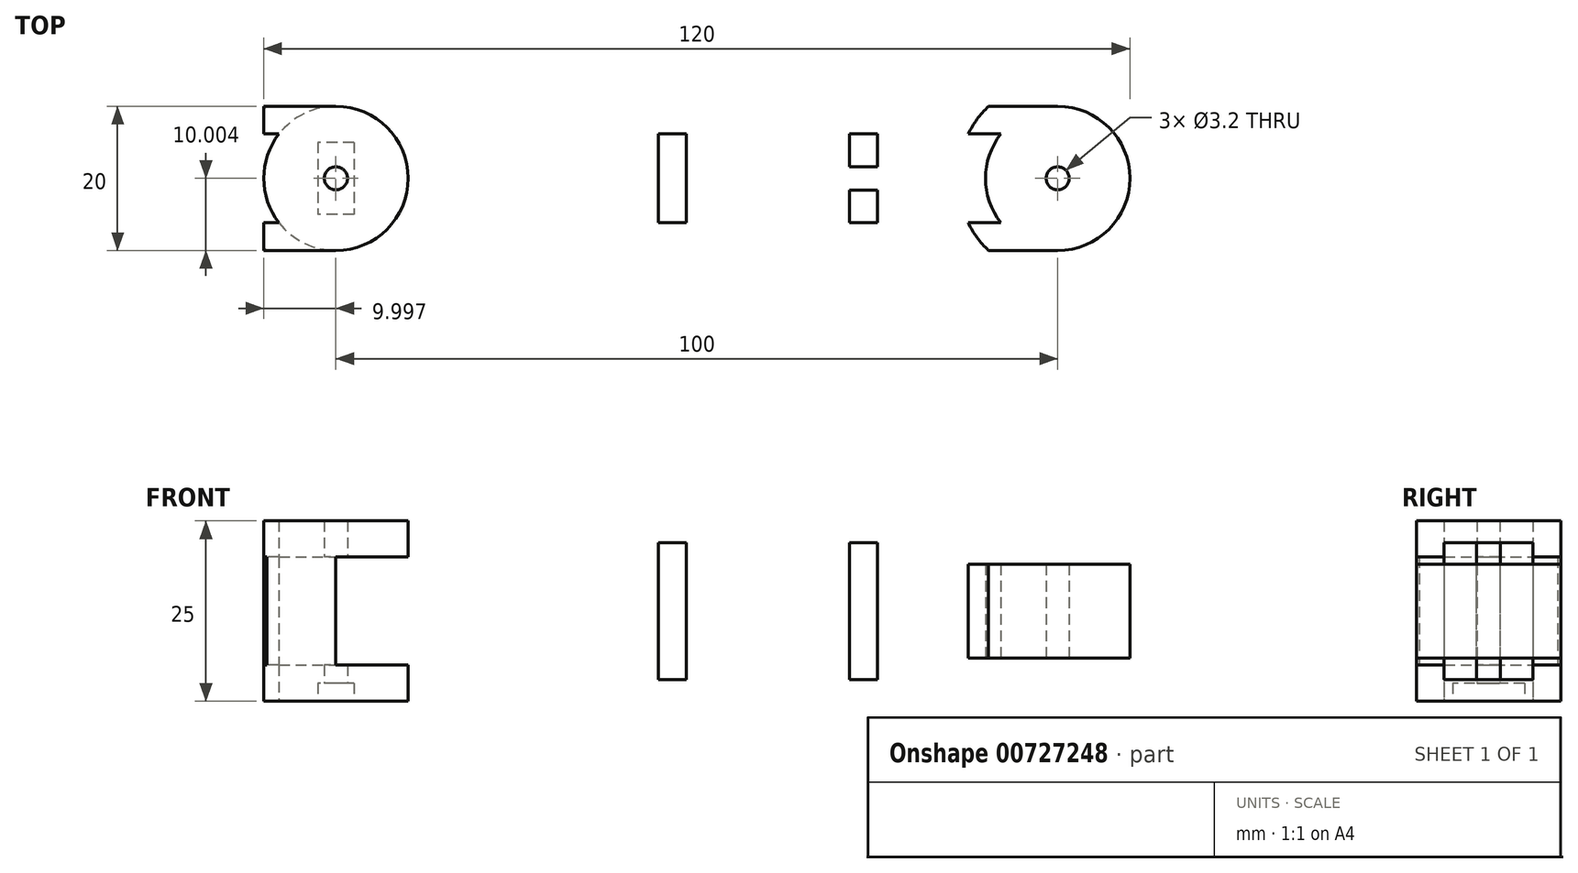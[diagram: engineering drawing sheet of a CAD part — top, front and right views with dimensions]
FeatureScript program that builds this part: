
annotation { "Feature Type Name" : "Feature", "Feature Type Description" : "" }
export const myFeature = defineFeature(function(context is Context, id is Id, definition is map)
    precondition{}
    {
        {
            var Q0;
            Q0=qCreatedBy(makeId("Top.planeOp"),FACE);
            var sketch = newSketch(context, id + "F0", { "sketchPlane" : qUnion([Q0])});
            skLineSegment(sketch, "E0.bottom", {"start": v(-96.42, 40.91) * mm, "end": v(23.58, 40.91) * mm});
            skLineSegment(sketch, "E0.top", {"start": v(-96.42, 20.91) * mm, "end": v(23.58, 20.91) * mm});
            skLineSegment(sketch, "E0.left", {"start": v(-96.42, 40.91) * mm, "end": v(-96.42, 20.91) * mm});
            skLineSegment(sketch, "E0.right", {"start": v(23.58, 40.91) * mm, "end": v(23.58, 20.91) * mm});
            skCircle(sketch, "E1", {"center": v(13.58, 30.91) * mm, "radius": 10 * mm});
            skPoint(sketch, "E1.centerSnap0", {"position": v(23.58, 30.91) * mm});
            skCircle(sketch, "E2", {"center": v(-86.42, 30.91) * mm, "radius": 10 * mm});
            skCircle(sketch, "E3", {"center": v(-86.42, 30.91) * mm, "radius": 1.6 * mm});
            skCircle(sketch, "E4", {"center": v(13.58, 30.91) * mm, "radius": 1.6 * mm});
            skLineSegment(sketch, "E5.0", {"start": v(-96.42, 37.06) * mm, "end": v(53.58, 37.06) * mm});
            skLineSegment(sketch, "E6.0", {"start": v(-96.42, 24.76) * mm, "end": v(53.58, 24.76) * mm});
            skCircle(sketch, "E7.0", {"center": v(-86.42, 30.91) * mm, "radius": 13.85 * mm});
            skCircle(sketch, "E8.0", {"center": v(13.58, 30.91) * mm, "radius": 13.85 * mm});
            skLineSegment(sketch, "E9", {"start": v(-15.27, 37.06) * mm, "end": v(-15.27, 24.76) * mm});
            skLineSegment(sketch, "E10", {"start": v(-11.42, 37.06) * mm, "end": v(-11.42, 24.76) * mm});
            skLineSegment(sketch, "E11", {"start": v(-41.72, 37.06) * mm, "end": v(-41.72, 24.76) * mm});
            skLineSegment(sketch, "E12", {"start": v(-37.87, 24.76) * mm, "end": v(-37.87, 37.06) * mm});
            skSolve(sketch);
        }
        {
            var Q0;
            {var subQ3=sQuery(id+"F0.wireOp",EDGE,"E7.0");var subQ4=sQuery(id+"F0.wireOp",EDGE,"E0.bottom");var subQ5=makeQuery(id+"F0.imprint","INTERSECT",VERTEX,{"disambiguationData":[OD(1.0)],"derivedFrom":[subQ4,subQ3]});Q0=makeQuery(id+"F0.imprint","IMPRINT",FACE,{"disambiguationData":[TD([[makeQuery(id+"F0.imprint","IMPRINT",EDGE,{"disambiguationData":[TD([[subQ5,-1.0]])],"derivedFrom":subQ4}),-1.0]])]});}
            var Q1;
            {var subQ0=sQuery(id+"F0.wireOp",EDGE,"E7.0");var subQ1=sQuery(id+"F0.wireOp",EDGE,"E0.bottom");var subQ2=makeQuery(id+"F0.imprint","INTERSECT",VERTEX,{"disambiguationData":[OD(1.0)],"derivedFrom":[subQ1,subQ0]});Q1=makeQuery(id+"F0.imprint","IMPRINT",FACE,{"disambiguationData":[TD([[makeQuery(id+"F0.imprint","IMPRINT",EDGE,{"disambiguationData":[TD([[subQ2,1.0]])],"derivedFrom":subQ1}),-1.0]])]});}
            var Q2;
            {var subQ0=sQuery(id+"F0.wireOp",EDGE,"E2");var subQ1=makeQuery(id+"F0.imprint","INTERSECT",VERTEX,{"derivedFrom":[sQuery(id+"F0.wireOp",EDGE,"E0.bottom"),subQ0]});Q2=makeQuery(id+"F0.imprint","IMPRINT",FACE,{"disambiguationData":[TD([[makeQuery(id+"F0.imprint","IMPRINT",EDGE,{"disambiguationData":[TD([[subQ1,1.0]])],"derivedFrom":subQ0}),1.0]])]});}
            var Q3;
            Q3=makeQuery(id+"F0.imprint","IMPRINT",FACE,{"disambiguationData":[TD([[makeQuery(id+"F0.imprint","IMPRINT",EDGE,{"derivedFrom":sQuery(id+"F0.wireOp",EDGE,"E3")}),-1.0]])]});
            var Q4;
            {var subQ0=sQuery(id+"F0.wireOp",EDGE,"E7.0");var subQ1=sQuery(id+"F0.wireOp",EDGE,"E0.top");var subQ2=makeQuery(id+"F0.imprint","INTERSECT",VERTEX,{"disambiguationData":[OD(1.0)],"derivedFrom":[subQ1,subQ0]});Q4=makeQuery(id+"F0.imprint","IMPRINT",FACE,{"disambiguationData":[TD([[makeQuery(id+"F0.imprint","IMPRINT",EDGE,{"disambiguationData":[TD([[subQ2,1.0]])],"derivedFrom":subQ1}),1.0]])]});}
            var Q5;
            {var subQ0=sQuery(id+"F0.wireOp",EDGE,"E2");var subQ1=makeQuery(id+"F0.imprint","INTERSECT",VERTEX,{"derivedFrom":[sQuery(id+"F0.wireOp",EDGE,"E0.top"),subQ0]});Q5=makeQuery(id+"F0.imprint","IMPRINT",FACE,{"disambiguationData":[TD([[makeQuery(id+"F0.imprint","IMPRINT",EDGE,{"disambiguationData":[TD([[subQ1,1.0]])],"derivedFrom":subQ0}),1.0]])]});}
            var Q6;
            {var subQ4=sQuery(id+"F0.wireOp",EDGE,"E7.0");var subQ6=sQuery(id+"F0.wireOp",EDGE,"E0.top");var subQ7=makeQuery(id+"F0.imprint","INTERSECT",VERTEX,{"disambiguationData":[OD(1.0)],"derivedFrom":[subQ6,subQ4]});Q6=makeQuery(id+"F0.imprint","IMPRINT",FACE,{"disambiguationData":[TD([[makeQuery(id+"F0.imprint","IMPRINT",EDGE,{"disambiguationData":[TD([[subQ7,-1.0]])],"derivedFrom":subQ6}),1.0]])]});}
            var Q7;
            {var subQ0=sQuery(id+"F0.wireOp",EDGE,"E11");Q7=makeQuery(id+"F0.imprint","IMPRINT",FACE,{"disambiguationData":[TD([[makeQuery(id+"F0.imprint","IMPRINT",EDGE,{"derivedFrom":subQ0}),1.0]])]});}
            var Q8;
            {var subQ0=sQuery(id+"F0.wireOp",EDGE,"E9");Q8=makeQuery(id+"F0.imprint","IMPRINT",FACE,{"disambiguationData":[TD([[makeQuery(id+"F0.imprint","IMPRINT",EDGE,{"derivedFrom":subQ0}),1.0]])]});}
            var Q9;
            Q9=makeQuery(id+"F0.imprint","IMPRINT",FACE,{"disambiguationData":[TD([[makeQuery(id+"F0.imprint","IMPRINT",EDGE,{"derivedFrom":sQuery(id+"F0.wireOp",EDGE,"E4")}),-1.0]])]});
            var Q10;
            {var subQ0=sQuery(id+"F0.wireOp",EDGE,"E1");var subQ1=makeQuery(id+"F0.imprint","INTERSECT",VERTEX,{"derivedFrom":[sQuery(id+"F0.wireOp",EDGE,"E0.bottom"),subQ0]});Q10=makeQuery(id+"F0.imprint","IMPRINT",FACE,{"disambiguationData":[TD([[makeQuery(id+"F0.imprint","IMPRINT",EDGE,{"disambiguationData":[TD([[subQ1,1.0]])],"derivedFrom":subQ0}),1.0]])]});}
            var Q11;
            {var subQ0=sQuery(id+"F0.wireOp",EDGE,"E8.0");var subQ1=sQuery(id+"F0.wireOp",EDGE,"E0.bottom");var subQ2=makeQuery(id+"F0.imprint","INTERSECT",VERTEX,{"disambiguationData":[OD(0.0)],"derivedFrom":[subQ1,subQ0]});Q11=makeQuery(id+"F0.imprint","IMPRINT",FACE,{"disambiguationData":[TD([[makeQuery(id+"F0.imprint","IMPRINT",EDGE,{"disambiguationData":[TD([[subQ2,-1.0]])],"derivedFrom":subQ1}),-1.0]])]});}
            var Q12;
            {var subQ0=sQuery(id+"F0.wireOp",EDGE,"E1");var subQ1=makeQuery(id+"F0.imprint","INTERSECT",VERTEX,{"derivedFrom":[sQuery(id+"F0.wireOp",EDGE,"E0.top"),subQ0]});Q12=makeQuery(id+"F0.imprint","IMPRINT",FACE,{"disambiguationData":[TD([[makeQuery(id+"F0.imprint","IMPRINT",EDGE,{"disambiguationData":[TD([[subQ1,1.0]])],"derivedFrom":subQ0}),1.0]])]});}
            var Q13;
            {var subQ0=sQuery(id+"F0.wireOp",EDGE,"E8.0");var subQ1=sQuery(id+"F0.wireOp",EDGE,"E0.top");var subQ2=makeQuery(id+"F0.imprint","INTERSECT",VERTEX,{"disambiguationData":[OD(0.0)],"derivedFrom":[subQ1,subQ0]});Q13=makeQuery(id+"F0.imprint","IMPRINT",FACE,{"disambiguationData":[TD([[makeQuery(id+"F0.imprint","IMPRINT",EDGE,{"disambiguationData":[TD([[subQ2,-1.0]])],"derivedFrom":subQ1}),1.0]])]});}
            extrude(context, id + "F1", {"entities" : qUnion([Q0, Q1, Q2, Q3, Q4, Q5, Q6, Q7, Q8, Q9, Q10, Q11, Q12, Q13]), "depth" : 25 * mm, "offsetDistance" : 25 * mm});
        }
        {
            var Q0;
            Q0=makeQuery(id+"F1.opExtrude","CAP_FACE",FACE,{"disambiguationData":[OSD([sQuery(id+"F0.wireOp",EDGE,"E0.bottom"),sQuery(id+"F0.wireOp",EDGE,"E0.top"),sQuery(id+"F0.wireOp",EDGE,"E1"),sQuery(id+"F0.wireOp",EDGE,"E2"),sQuery(id+"F0.wireOp",EDGE,"E3"),sQuery(id+"F0.wireOp",EDGE,"E4"),sQuery(id+"F0.wireOp",EDGE,"E5.0"),sQuery(id+"F0.wireOp",EDGE,"E6.0"),sQuery(id+"F0.wireOp",EDGE,"E9"),sQuery(id+"F0.wireOp",EDGE,"E10"),sQuery(id+"F0.wireOp",EDGE,"E11"),sQuery(id+"F0.wireOp",EDGE,"E12")])],"isStart":false});
            var sketch = newSketch(context, id + "F2", { "sketchPlane" : qUnion([Q0])});
            skLineSegment(sketch, "E13.bottom", {"start": v(-41.72, 37.06) * mm, "end": v(-37.87, 37.06) * mm});
            skLineSegment(sketch, "E13.top", {"start": v(-41.72, 24.76) * mm, "end": v(-37.87, 24.76) * mm});
            skLineSegment(sketch, "E13.left", {"start": v(-41.72, 37.06) * mm, "end": v(-41.72, 24.76) * mm});
            skLineSegment(sketch, "E13.right", {"start": v(-37.87, 37.06) * mm, "end": v(-37.87, 24.76) * mm});
            skLineSegment(sketch, "E14.bottom", {"start": v(-15.27, 37.06) * mm, "end": v(-11.42, 37.06) * mm});
            skLineSegment(sketch, "E14.top", {"start": v(-15.27, 24.76) * mm, "end": v(-11.42, 24.76) * mm});
            skLineSegment(sketch, "E14.left", {"start": v(-15.27, 37.06) * mm, "end": v(-15.27, 24.76) * mm});
            skLineSegment(sketch, "E14.right", {"start": v(-11.42, 37.06) * mm, "end": v(-11.42, 24.76) * mm});
            skSolve(sketch);
        }
        {
            var Q0;
            Q0 = qSketchRegion(id + "F2", true);
            extrude(context, id + "F3", {"entities" : qUnion([Q0]), "operationType" : NewBodyOperationType.REMOVE, "oppositeDirection" : true, "depth" : 3 * mm, "offsetDistance" : 25 * mm});
        }
        {
            var Q0;
            Q0=makeQuery(id+"F1.opExtrude","CAP_FACE",FACE,{"disambiguationData":[OSD([sQuery(id+"F0.wireOp",EDGE,"E0.bottom"),sQuery(id+"F0.wireOp",EDGE,"E0.top"),sQuery(id+"F0.wireOp",EDGE,"E1"),sQuery(id+"F0.wireOp",EDGE,"E2"),sQuery(id+"F0.wireOp",EDGE,"E3"),sQuery(id+"F0.wireOp",EDGE,"E4"),sQuery(id+"F0.wireOp",EDGE,"E5.0"),sQuery(id+"F0.wireOp",EDGE,"E6.0"),sQuery(id+"F0.wireOp",EDGE,"E9"),sQuery(id+"F0.wireOp",EDGE,"E10"),sQuery(id+"F0.wireOp",EDGE,"E11"),sQuery(id+"F0.wireOp",EDGE,"E12")])],"isStart":true});
            var sketch = newSketch(context, id + "F4", { "sketchPlane" : qUnion([Q0])});
            skLineSegment(sketch, "E15.bottom", {"start": v(-11.42, -37.06) * mm, "end": v(-15.27, -37.06) * mm});
            skLineSegment(sketch, "E15.top", {"start": v(-11.42, -24.76) * mm, "end": v(-15.27, -24.76) * mm});
            skLineSegment(sketch, "E15.left", {"start": v(-11.42, -37.06) * mm, "end": v(-11.42, -24.76) * mm});
            skLineSegment(sketch, "E15.right", {"start": v(-15.27, -37.06) * mm, "end": v(-15.27, -24.76) * mm});
            skLineSegment(sketch, "E16.bottom", {"start": v(-37.87, -37.06) * mm, "end": v(-41.72, -37.06) * mm});
            skLineSegment(sketch, "E16.top", {"start": v(-37.87, -24.76) * mm, "end": v(-41.72, -24.76) * mm});
            skLineSegment(sketch, "E16.left", {"start": v(-37.87, -37.06) * mm, "end": v(-37.87, -24.76) * mm});
            skLineSegment(sketch, "E16.right", {"start": v(-41.72, -37.06) * mm, "end": v(-41.72, -24.76) * mm});
            skSolve(sketch);
        }
        {
            var Q0;
            Q0 = qSketchRegion(id + "F4", true);
            extrude(context, id + "F5", {"entities" : qUnion([Q0]), "operationType" : NewBodyOperationType.REMOVE, "oppositeDirection" : true, "depth" : 3 * mm, "offsetDistance" : 25 * mm});
        }
        {
            var Q0;
            Q0=makeQuery(id+"F1.opExtrude","CAP_FACE",FACE,{"disambiguationData":[OSD([sQuery(id+"F0.wireOp",EDGE,"E0.bottom"),sQuery(id+"F0.wireOp",EDGE,"E0.top"),sQuery(id+"F0.wireOp",EDGE,"E1"),sQuery(id+"F0.wireOp",EDGE,"E2"),sQuery(id+"F0.wireOp",EDGE,"E3"),sQuery(id+"F0.wireOp",EDGE,"E4"),sQuery(id+"F0.wireOp",EDGE,"E5.0"),sQuery(id+"F0.wireOp",EDGE,"E6.0"),sQuery(id+"F0.wireOp",EDGE,"E9"),sQuery(id+"F0.wireOp",EDGE,"E10"),sQuery(id+"F0.wireOp",EDGE,"E11"),sQuery(id+"F0.wireOp",EDGE,"E12")])],"isStart":true});
            var sketch = newSketch(context, id + "F6", { "sketchPlane" : qUnion([Q0])});
            skPoint(sketch, "E17", {"position": v(-20.27, -39.81) * mm});
            skPoint(sketch, "E17.positionSnap0", {"position": v(-15.27, -39.81) * mm});
            skSolve(sketch);
        }
        {
            var Q0;
            {var subQ0=sQuery(id+"F0.wireOp",EDGE,"E1");var subQ1=makeQuery(id+"F0.imprint","INTERSECT",VERTEX,{"derivedFrom":[sQuery(id+"F0.wireOp",EDGE,"E0.top"),subQ0]});Q0=makeQuery(id+"F0.imprint","IMPRINT",FACE,{"disambiguationData":[TD([[makeQuery(id+"F0.imprint","IMPRINT",EDGE,{"disambiguationData":[TD([[subQ1,1.0]])],"derivedFrom":subQ0}),1.0]])]});}
            var Q1;
            Q1=makeQuery(id+"F0.imprint","IMPRINT",FACE,{"disambiguationData":[TD([[makeQuery(id+"F0.imprint","IMPRINT",EDGE,{"derivedFrom":sQuery(id+"F0.wireOp",EDGE,"E4")}),-1.0]])]});
            var Q2;
            {var subQ0=sQuery(id+"F0.wireOp",EDGE,"E1");var subQ1=makeQuery(id+"F0.imprint","INTERSECT",VERTEX,{"derivedFrom":[sQuery(id+"F0.wireOp",EDGE,"E0.bottom"),subQ0]});Q2=makeQuery(id+"F0.imprint","IMPRINT",FACE,{"disambiguationData":[TD([[makeQuery(id+"F0.imprint","IMPRINT",EDGE,{"disambiguationData":[TD([[subQ1,1.0]])],"derivedFrom":subQ0}),1.0]])]});}
            var Q3;
            {var subQ0=sQuery(id+"F0.wireOp",EDGE,"E8.0");var subQ1=sQuery(id+"F0.wireOp",EDGE,"E0.bottom");var subQ2=makeQuery(id+"F0.imprint","INTERSECT",VERTEX,{"disambiguationData":[OD(0.0)],"derivedFrom":[subQ1,subQ0]});Q3=makeQuery(id+"F0.imprint","IMPRINT",FACE,{"disambiguationData":[TD([[makeQuery(id+"F0.imprint","IMPRINT",EDGE,{"disambiguationData":[TD([[subQ2,-1.0]])],"derivedFrom":subQ1}),-1.0]])]});}
            var Q4;
            {var subQ0=sQuery(id+"F0.wireOp",EDGE,"E8.0");var subQ1=sQuery(id+"F0.wireOp",EDGE,"E0.top");var subQ2=makeQuery(id+"F0.imprint","INTERSECT",VERTEX,{"disambiguationData":[OD(0.0)],"derivedFrom":[subQ1,subQ0]});Q4=makeQuery(id+"F0.imprint","IMPRINT",FACE,{"disambiguationData":[TD([[makeQuery(id+"F0.imprint","IMPRINT",EDGE,{"disambiguationData":[TD([[subQ2,-1.0]])],"derivedFrom":subQ1}),1.0]])]});}
            extrude(context, id + "F7", {"entities" : qUnion([Q0, Q1, Q2, Q3, Q4]), "operationType" : NewBodyOperationType.REMOVE, "depth" : 25 * mm, "offsetDistance" : 25 * mm, "hasSecondDirection" : true, "secondDirectionOppositeDirection" : false, "secondDirectionDepth" : 19 * mm});
        }
        {
            var Q0;
            Q0=makeQuery(id+"F0.imprint","IMPRINT",FACE,{"disambiguationData":[TD([[makeQuery(id+"F0.imprint","IMPRINT",EDGE,{"derivedFrom":sQuery(id+"F0.wireOp",EDGE,"E4")}),-1.0]])]});
            var Q1;
            {var subQ0=sQuery(id+"F0.wireOp",EDGE,"E8.0");var subQ1=sQuery(id+"F0.wireOp",EDGE,"E0.bottom");var subQ2=makeQuery(id+"F0.imprint","INTERSECT",VERTEX,{"disambiguationData":[OD(0.0)],"derivedFrom":[subQ1,subQ0]});Q1=makeQuery(id+"F0.imprint","IMPRINT",FACE,{"disambiguationData":[TD([[makeQuery(id+"F0.imprint","IMPRINT",EDGE,{"disambiguationData":[TD([[subQ2,-1.0]])],"derivedFrom":subQ1}),-1.0]])]});}
            var Q2;
            {var subQ0=sQuery(id+"F0.wireOp",EDGE,"E8.0");var subQ1=sQuery(id+"F0.wireOp",EDGE,"E0.top");var subQ2=makeQuery(id+"F0.imprint","INTERSECT",VERTEX,{"disambiguationData":[OD(0.0)],"derivedFrom":[subQ1,subQ0]});Q2=makeQuery(id+"F0.imprint","IMPRINT",FACE,{"disambiguationData":[TD([[makeQuery(id+"F0.imprint","IMPRINT",EDGE,{"disambiguationData":[TD([[subQ2,-1.0]])],"derivedFrom":subQ1}),1.0]])]});}
            var Q3;
            {var subQ0=sQuery(id+"F0.wireOp",EDGE,"E1");var subQ1=makeQuery(id+"F0.imprint","INTERSECT",VERTEX,{"derivedFrom":[sQuery(id+"F0.wireOp",EDGE,"E0.top"),subQ0]});Q3=makeQuery(id+"F0.imprint","IMPRINT",FACE,{"disambiguationData":[TD([[makeQuery(id+"F0.imprint","IMPRINT",EDGE,{"disambiguationData":[TD([[subQ1,1.0]])],"derivedFrom":subQ0}),1.0]])]});}
            var Q4;
            {var subQ0=sQuery(id+"F0.wireOp",EDGE,"E1");var subQ1=makeQuery(id+"F0.imprint","INTERSECT",VERTEX,{"derivedFrom":[sQuery(id+"F0.wireOp",EDGE,"E0.bottom"),subQ0]});Q4=makeQuery(id+"F0.imprint","IMPRINT",FACE,{"disambiguationData":[TD([[makeQuery(id+"F0.imprint","IMPRINT",EDGE,{"disambiguationData":[TD([[subQ1,1.0]])],"derivedFrom":subQ0}),1.0]])]});}
            extrude(context, id + "F8", {"entities" : qUnion([Q0, Q1, Q2, Q3, Q4]), "operationType" : NewBodyOperationType.REMOVE, "depth" : 6 * mm, "offsetDistance" : 25 * mm});
        }
        {
            var Q0;
            Q0=makeQuery(id+"F0.imprint","IMPRINT",FACE,{"disambiguationData":[TD([[makeQuery(id+"F0.imprint","IMPRINT",EDGE,{"derivedFrom":sQuery(id+"F0.wireOp",EDGE,"E3")}),-1.0]])]});
            var Q1;
            {var subQ0=sQuery(id+"F0.wireOp",EDGE,"E2");var subQ1=makeQuery(id+"F0.imprint","INTERSECT",VERTEX,{"derivedFrom":[sQuery(id+"F0.wireOp",EDGE,"E0.top"),subQ0]});Q1=makeQuery(id+"F0.imprint","IMPRINT",FACE,{"disambiguationData":[TD([[makeQuery(id+"F0.imprint","IMPRINT",EDGE,{"disambiguationData":[TD([[subQ1,1.0]])],"derivedFrom":subQ0}),1.0]])]});}
            var Q2;
            {var subQ0=sQuery(id+"F0.wireOp",EDGE,"E2");var subQ1=makeQuery(id+"F0.imprint","INTERSECT",VERTEX,{"derivedFrom":[sQuery(id+"F0.wireOp",EDGE,"E0.bottom"),subQ0]});Q2=makeQuery(id+"F0.imprint","IMPRINT",FACE,{"disambiguationData":[TD([[makeQuery(id+"F0.imprint","IMPRINT",EDGE,{"disambiguationData":[TD([[subQ1,1.0]])],"derivedFrom":subQ0}),1.0]])]});}
            var Q3;
            {var subQ0=sQuery(id+"F0.wireOp",EDGE,"E7.0");var subQ1=sQuery(id+"F0.wireOp",EDGE,"E0.bottom");var subQ2=makeQuery(id+"F0.imprint","INTERSECT",VERTEX,{"disambiguationData":[OD(1.0)],"derivedFrom":[subQ1,subQ0]});Q3=makeQuery(id+"F0.imprint","IMPRINT",FACE,{"disambiguationData":[TD([[makeQuery(id+"F0.imprint","IMPRINT",EDGE,{"disambiguationData":[TD([[subQ2,1.0]])],"derivedFrom":subQ1}),-1.0]])]});}
            var Q4;
            {var subQ0=sQuery(id+"F0.wireOp",EDGE,"E7.0");var subQ1=sQuery(id+"F0.wireOp",EDGE,"E0.top");var subQ2=makeQuery(id+"F0.imprint","INTERSECT",VERTEX,{"disambiguationData":[OD(1.0)],"derivedFrom":[subQ1,subQ0]});Q4=makeQuery(id+"F0.imprint","IMPRINT",FACE,{"disambiguationData":[TD([[makeQuery(id+"F0.imprint","IMPRINT",EDGE,{"disambiguationData":[TD([[subQ2,1.0]])],"derivedFrom":subQ1}),1.0]])]});}
            extrude(context, id + "F9", {"entities" : qUnion([Q0, Q1, Q2, Q3, Q4]), "operationType" : NewBodyOperationType.REMOVE, "depth" : 20 * mm, "offsetDistance" : 25 * mm, "hasSecondDirection" : true, "secondDirectionOppositeDirection" : false, "secondDirectionDepth" : 5 * mm});
        }
        {
            var Q0;
            Q0=makeQuery(id+"F0.imprint","IMPRINT",FACE,{"disambiguationData":[TD([[makeQuery(id+"F0.imprint","IMPRINT",EDGE,{"derivedFrom":sQuery(id+"F0.wireOp",EDGE,"E3")}),-1.0]])]});
            var sketch = newSketch(context, id + "F10", { "sketchPlane" : qUnion([Q0])});
            skLineSegment(sketch, "E18.bottom", {"start": v(-83.92, 35.91) * mm, "end": v(-88.92, 35.91) * mm});
            skLineSegment(sketch, "E18.top", {"start": v(-83.92, 25.91) * mm, "end": v(-88.92, 25.91) * mm});
            skLineSegment(sketch, "E18.left", {"start": v(-83.92, 35.91) * mm, "end": v(-83.92, 25.91) * mm});
            skLineSegment(sketch, "E18.right", {"start": v(-88.92, 35.91) * mm, "end": v(-88.92, 25.91) * mm});
            skPoint(sketch, "E18.middle", {"position": v(-86.42, 30.91) * mm});
            skSolve(sketch);
        }
        {
            var Q0;
            Q0 = qSketchRegion(id + "F10", true);
            extrude(context, id + "F11", {"entities" : qUnion([Q0]), "operationType" : NewBodyOperationType.REMOVE, "depth" : 2.5 * mm, "offsetDistance" : 25 * mm});
        }
        {
            var Q0;
            {var subQ0=sQuery(id+"F0.wireOp",EDGE,"E5.0");var subQ1=sQuery(id+"F0.wireOp",EDGE,"E1");var subQ2=makeQuery(id+"F0.imprint","INTERSECT",VERTEX,{"disambiguationData":[OD(1.0)],"derivedFrom":[subQ1,subQ0]});Q0=makeQuery(id+"F6.imprint","IMPRINT",FACE,{"disambiguationData":[TD([[makeQuery(id+"F6.imprint","IMPRINT",EDGE,{"derivedFrom":makeQuery(id+"F1.opExtrude","CAP_EDGE",EDGE,{"disambiguationData":[OSD([subQ1]),TDD([makeQuery(id+"F0.imprint","IMPRINT",EDGE,{"disambiguationData":[TD([[subQ2,-1.0]])],"derivedFrom":subQ1})])],"isStart":true})}),1.0]])]});}
            var sketch = newSketch(context, id + "F12", { "sketchPlane" : qUnion([Q0])});
            skPoint(sketch, "E19", {"position": v(-20.27, -30.91) * mm});
            skCircle(sketch, "E20", {"center": v(-20.27, -30.91) * mm, "radius": 6 * mm});
            skCircle(sketch, "E21", {"center": v(-20.27, -30.91) * mm, "radius": 3.5 * mm, "construction": true});
            skCircle(sketch, "E22", {"center": v(13.58, -30.91) * mm, "radius": 30 * mm});
            skSolve(sketch);
        }
        {
            var Q0;
            Q0=makeQuery(id+"F3.boolean.opBoolean","COPY",FACE,{"derivedFrom":makeQuery(id+"F3.opExtrude","CAP_FACE",FACE,{"disambiguationData":[OSD([sQuery(id+"F2.wireOp",EDGE,"E14.bottom"),sQuery(id+"F2.wireOp",EDGE,"E14.top"),sQuery(id+"F2.wireOp",EDGE,"E14.left"),sQuery(id+"F2.wireOp",EDGE,"E14.right")])],"isStart":false})});
            var sketch = newSketch(context, id + "F13", { "sketchPlane" : qUnion([Q0])});
            skLineSegment(sketch, "E23.bottom", {"start": v(-10.3, 29.27) * mm, "end": v(-16.4, 29.27) * mm});
            skLineSegment(sketch, "E23.top", {"start": v(-10.3, 32.55) * mm, "end": v(-16.4, 32.55) * mm});
            skLineSegment(sketch, "E23.left", {"start": v(-10.3, 29.27) * mm, "end": v(-10.3, 32.55) * mm});
            skLineSegment(sketch, "E23.right", {"start": v(-16.4, 29.27) * mm, "end": v(-16.4, 32.55) * mm});
            skPoint(sketch, "E23.middle", {"position": v(-13.35, 30.91) * mm});
            skPoint(sketch, "E23.middle.positionSnap0", {"position": v(-15.27, 30.91) * mm});
            skPoint(sketch, "E23.middle.positionSnap1", {"position": v(-13.35, 37.06) * mm});
            skPoint(sketch, "E23.centerSnap0", {"position": v(-15.27, 30.91) * mm});
            skPoint(sketch, "E23.centerSnap1", {"position": v(-13.35, 37.06) * mm});
            skSolve(sketch);
        }
        {
            var Q0;
            Q0 = qSketchRegion(id + "F13", true);
            extrude(context, id + "F14", {"entities" : qUnion([Q0]), "operationType" : NewBodyOperationType.REMOVE, "oppositeDirection" : true, "depth" : 25 * mm, "offsetDistance" : 25 * mm});
        }
    });
